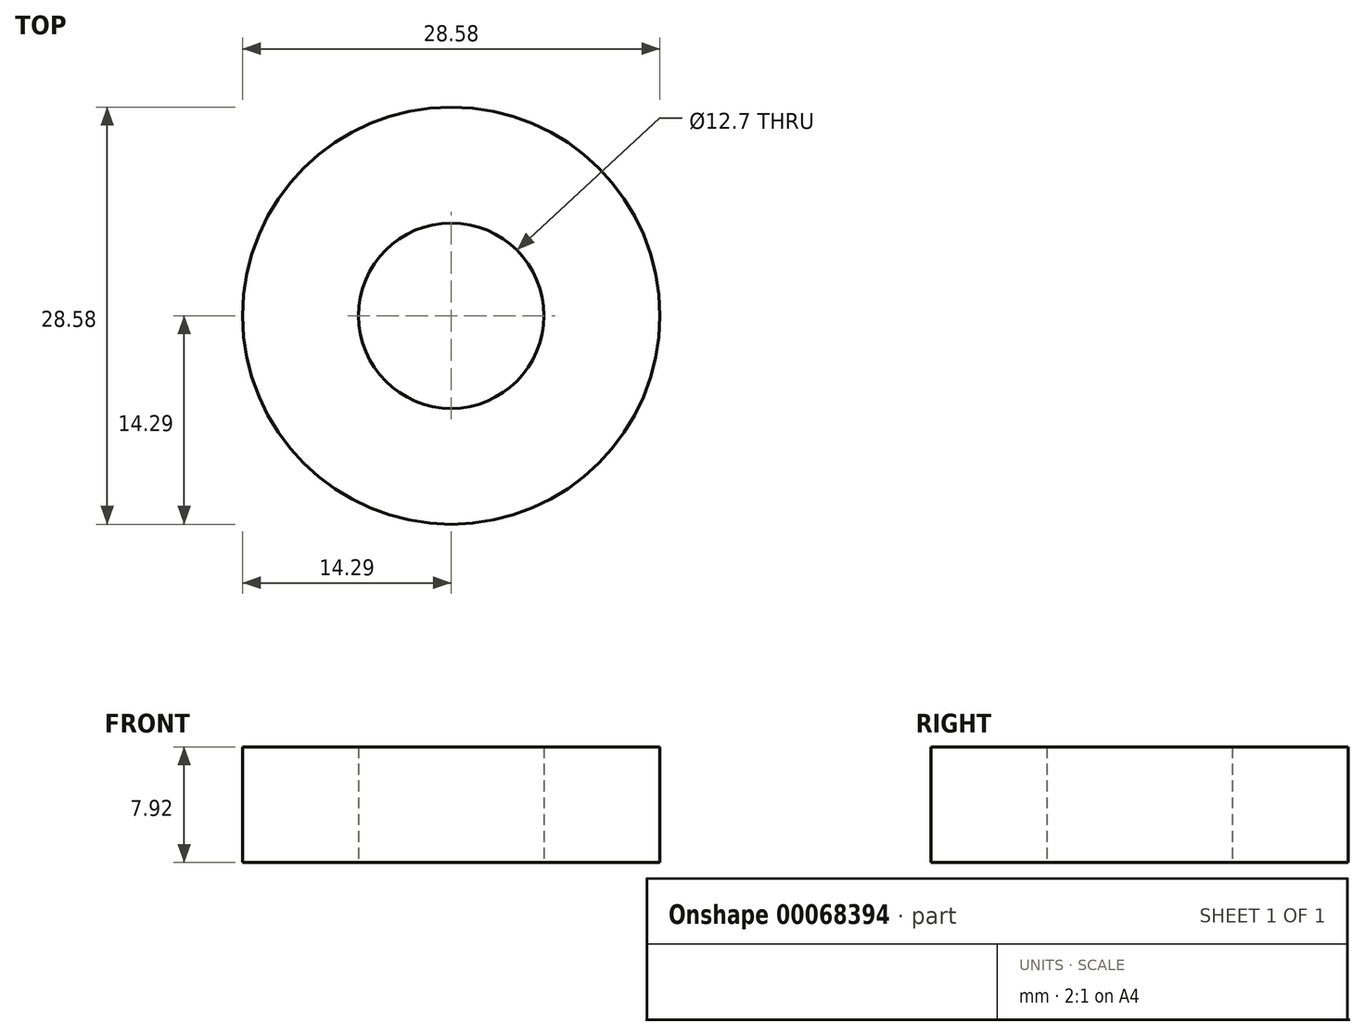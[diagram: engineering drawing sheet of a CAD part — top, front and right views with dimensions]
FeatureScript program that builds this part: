
annotation { "Feature Type Name" : "Feature", "Feature Type Description" : "" }
export const myFeature = defineFeature(function(context is Context, id is Id, definition is map)
    precondition{}
    {
        {
            var Q0;
            Q0=qCreatedBy(makeId("Top.planeOp"),FACE);
            var sketch = newSketch(context, id + "F0", { "sketchPlane" : qUnion([Q0])});
            skCircle(sketch, "E0", {"center": v(0, 0) * mm, "radius": 14.29 * mm});
            skCircle(sketch, "E1", {"center": v(0, 0) * mm, "radius": 6.35 * mm});
            skSolve(sketch);
        }
        {
            var Q0;
            Q0 = qSketchRegion(id + "F0", true);
            extrude(context, id + "F1", {"entities" : qUnion([Q0]), "depth" : 7.92 * mm});
        }
    });
